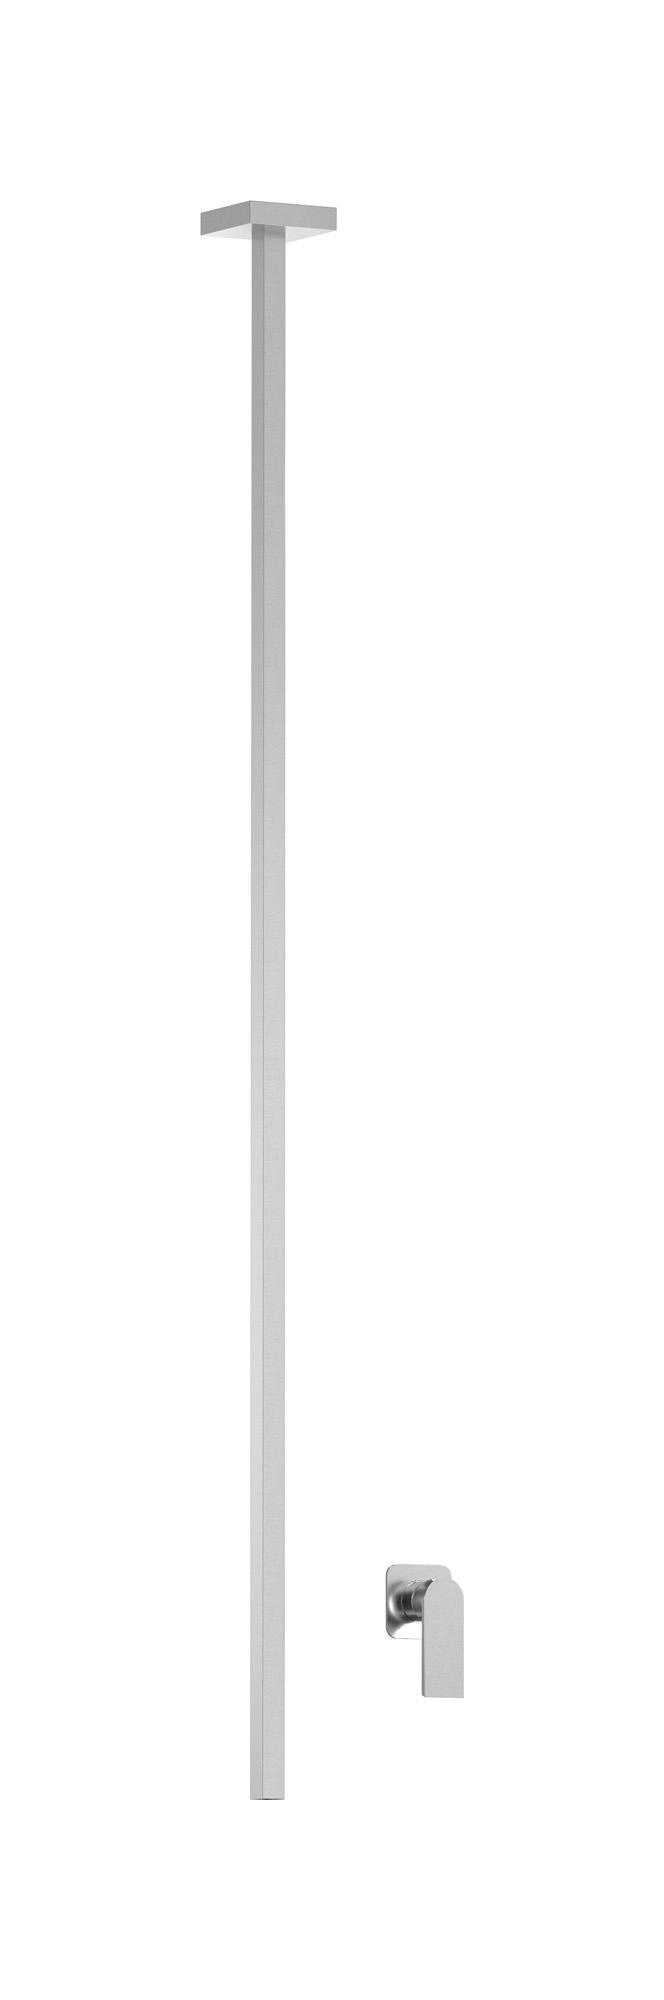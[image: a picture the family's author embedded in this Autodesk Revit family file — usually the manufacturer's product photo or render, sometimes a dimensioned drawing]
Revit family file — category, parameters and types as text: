
# Revit family: K3210
name_source: partatom
category: Apparecchi idraulici
units: mm (PartAtom-declared; Revit-internal decimal feet)

## family parameters
Basato su piano di lavoro = No
Condiviso = No
Mantieni orientamento annotazione = No
Numero OmniClass = 23.45.55.17
Punto di calcolo locali = No
Quota connettore circolare = Usa diametro
Sempre verticale = Sì
Taglio con vuoti quando caricato = No
Tipo di parte = Normale
Titolo OmniClass = Mixing Faucets

## types (4) — shared parameters
Cold water inlet = 10 mm  [stored 0.0328084 ft]
Commenti sul tipo = Wall mixer
Connessione CW = No
Connessione HW = No
Connessione di scarico = No
Connessione di ventilazione = No
Descrizione = Ceiling spout with wall mounted mixer
Hot water inlet = 10 mm  [stored 0.0328084 ft]
Produttore = IB Rubinetterie S.p.A.
URL = https://www.weareib.it
zero-valued in all types: Prospetto di default

## per-type parameters (varying)
| type | Finishes surface | Immagine tipo | Modello |
| Chrome | IB_Chrome | K3210CC.jpg | K3210CC |
| Brushed nickel | IB_Brushed nickel | K3210SS.jpg | K3210SS |
| Matt black | IB_matt black | K3210NP.jpg | K3210NP |
| Matt white | IB_matt white | K3210BO.jpg | K3210BO |

note: [stored X ft] marks values corroborated as IEEE doubles in the binary element streams (Revit-internal decimal feet)
